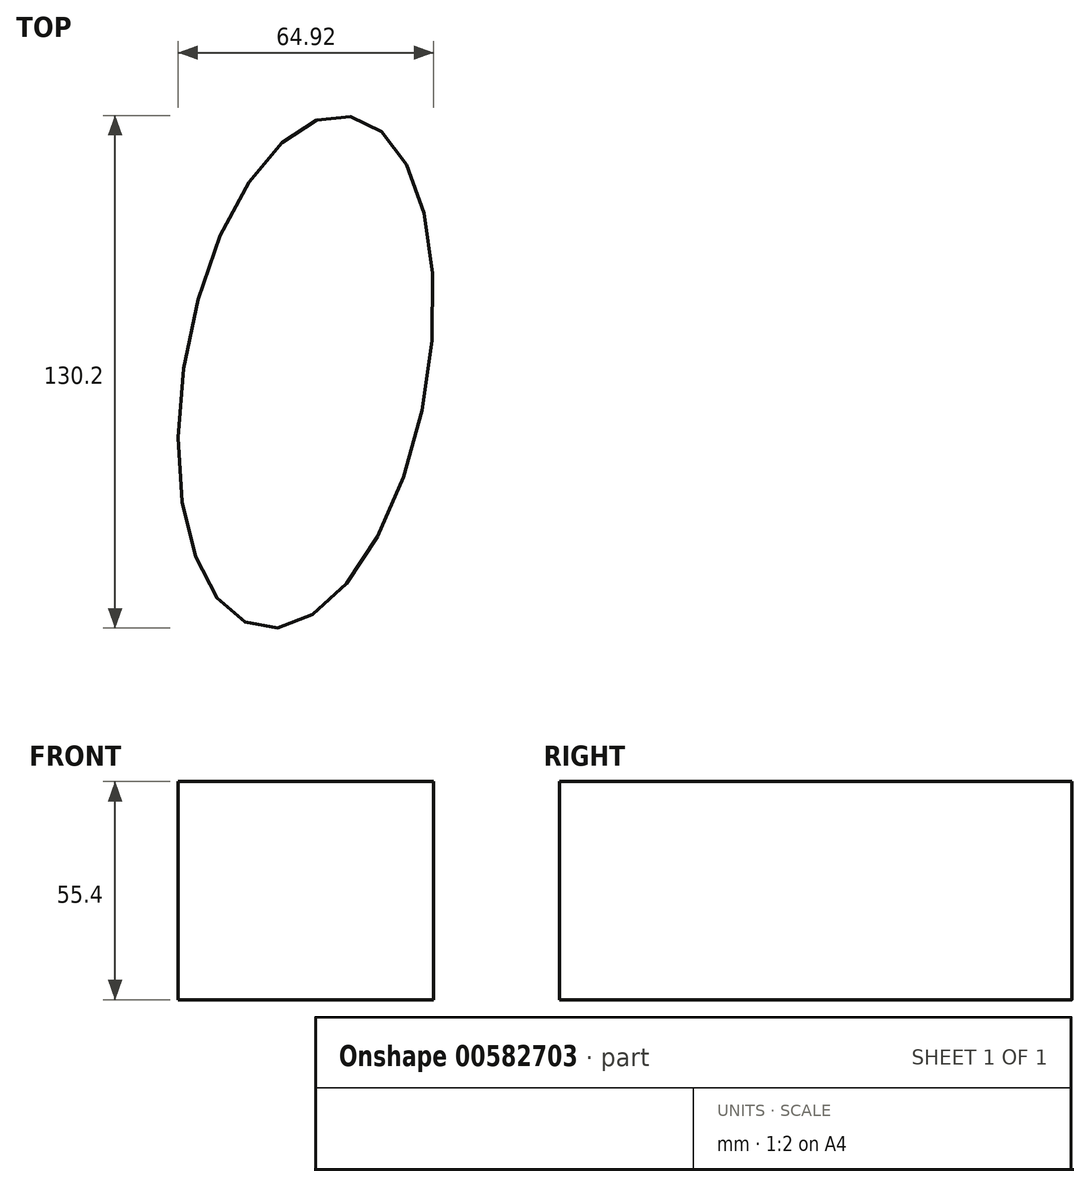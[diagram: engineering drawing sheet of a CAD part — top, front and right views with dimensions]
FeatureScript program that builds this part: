
annotation { "Feature Type Name" : "Feature", "Feature Type Description" : "" }
export const myFeature = defineFeature(function(context is Context, id is Id, definition is map)
    precondition{}
    {
        {
            var Q0;
            Q0=qCreatedBy(makeId("Top.planeOp"),FACE);
            var sketch = newSketch(context, id + "F0", { "sketchPlane" : qUnion([Q0])});
            skCircle(sketch, "E0", {"center": v(0, 0) * mm, "radius": 39.87 * mm});
            skSolve(sketch);
        }
        {
            var Q0;
            Q0=sQuery(id+"F0.wireOp",EDGE,"E0");
            extrude(context, id + "F1", {"bodyType" : ToolBodyType.SURFACE, "surfaceEntities" : qUnion([Q0]), "depth" : 80 * mm, "offsetDistance" : 25.4 * mm});
        }
        {
            var Q0;
            Q0=qCreatedBy(makeId("Top.planeOp"),FACE);
            var sketch = newSketch(context, id + "F2", { "sketchPlane" : qUnion([Q0])});
            skEllipse(sketch, "E1", {"center": v(0, 0) * mm, "majorRadius": 65.87 * mm, "minorRadius": 30.86 * mm, "majorAxis": v(0.17, 0.98)});
            skSolve(sketch);
        }
        {
            var Q0;
            Q0 = qSketchRegion(id + "F2", true);
            extrude(context, id + "F3", {"entities" : qUnion([Q0]), "depth" : 30 * mm, "offsetDistance" : 25.4 * mm});
        }
        {
            var Q0;
            Q0=makeQuery(id+"F3.opExtrude","CAP_FACE",FACE,{"disambiguationData":[OSD([sQuery(id+"F2.wireOp",EDGE,"E1")])],"isStart":true});
            extrude(context, id + "F4", {"entities" : qUnion([Q0]), "operationType" : NewBodyOperationType.ADD, "depth" : 25.4 * mm, "offsetDistance" : 25.4 * mm, "hasSecondDirection" : true, "secondDirectionOppositeDirection" : true, "secondDirectionDepth" : 25.4 * mm});
        }
    });
